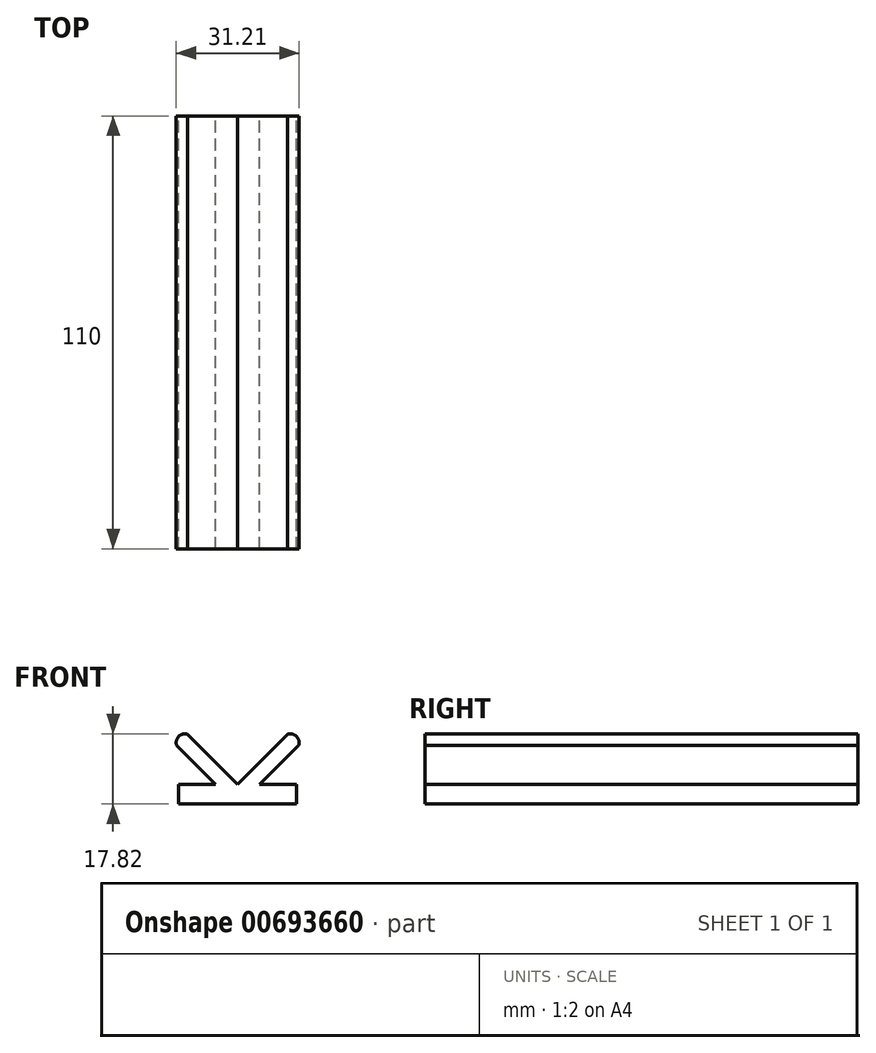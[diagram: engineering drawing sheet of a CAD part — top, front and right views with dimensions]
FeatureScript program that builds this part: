
annotation { "Feature Type Name" : "Feature", "Feature Type Description" : "" }
export const myFeature = defineFeature(function(context is Context, id is Id, definition is map)
    precondition{}
    {
        {
            var Q0;
            Q0=qCreatedBy(makeId("Front.planeOp"),FACE);
            var sketch = newSketch(context, id + "F0", { "sketchPlane" : qUnion([Q0])});
            skLineSegment(sketch, "E0.bottom", {"start": v(-22.98, 0) * mm, "end": v(7.02, 0) * mm});
            skLineSegment(sketch, "E0.top", {"start": v(-22.98, 5) * mm, "end": v(7.02, 5) * mm});
            skLineSegment(sketch, "E0.left", {"start": v(-22.98, 0) * mm, "end": v(-22.98, 5) * mm});
            skLineSegment(sketch, "E0.right", {"start": v(7.02, 0) * mm, "end": v(7.02, 5) * mm});
            skLineSegment(sketch, "E1", {"start": v(-22.98, 5) * mm, "end": v(7.02, 0) * mm, "construction": true});
            skLineSegment(sketch, "E2", {"start": v(7.02, 5) * mm, "end": v(-22.98, 0) * mm, "construction": true});
            skLineSegment(sketch, "E3", {"start": v(-7.98, 2.5) * mm, "end": v(-7.98, 20.22) * mm, "construction": true});
            skLineSegment(sketch, "E4", {"start": v(-7.98, 5) * mm, "end": v(-20.7, 17.73) * mm});
            skLineSegment(sketch, "E5.MirrorCS", {"start": v(-7.98, 5) * mm, "end": v(4.75, 17.73) * mm});
            skLineSegment(sketch, "E6", {"start": v(-23.5, 14.94) * mm, "end": v(-13.56, 5) * mm});
            skArc(sketch, "E7", {"start": v(-20.7, 17.73) * mm, "mid": v(-22.92, 17.16) * mm, "end": v(-23.5, 14.94) * mm});
            skLineSegment(sketch, "E8.MirrorCS", {"start": v(7.54, 14.94) * mm, "end": v(-2.4, 5) * mm});
            skArc(sketch, "E9.MirrorCS", {"start": v(4.75, 17.73) * mm, "mid": v(6.97, 17.16) * mm, "end": v(7.54, 14.94) * mm});
            skSolve(sketch);
        }
        {
            var Q0;
            Q0=makeQuery(id+"F0.imprint","IMPRINT",FACE,{"disambiguationData":[TD([[makeQuery(id+"F0.imprint","IMPRINT",EDGE,{"derivedFrom":sQuery(id+"F0.wireOp",EDGE,"E0.bottom")}),1.0]])]});
            extrude(context, id + "F1", {"entities" : qUnion([Q0]), "depth" : 110 * mm, "offsetDistance" : 25 * mm});
        }
        {
            var Q0;
            {var subQ0=sQuery(id+"F0.wireOp",EDGE,"E4");Q0=makeQuery(id+"F0.imprint","IMPRINT",FACE,{"disambiguationData":[TD([[makeQuery(id+"F0.imprint","IMPRINT",EDGE,{"derivedFrom":subQ0}),1.0]])]});}
            var Q1;
            {var subQ0=sQuery(id+"F0.wireOp",EDGE,"E5.MirrorCS");Q1=makeQuery(id+"F0.imprint","IMPRINT",FACE,{"disambiguationData":[TD([[makeQuery(id+"F0.imprint","IMPRINT",EDGE,{"derivedFrom":subQ0}),-1.0]])]});}
            extrude(context, id + "F2", {"entities" : qUnion([Q0, Q1]), "operationType" : NewBodyOperationType.ADD, "depth" : 110 * mm, "offsetDistance" : 25 * mm});
        }
    });
